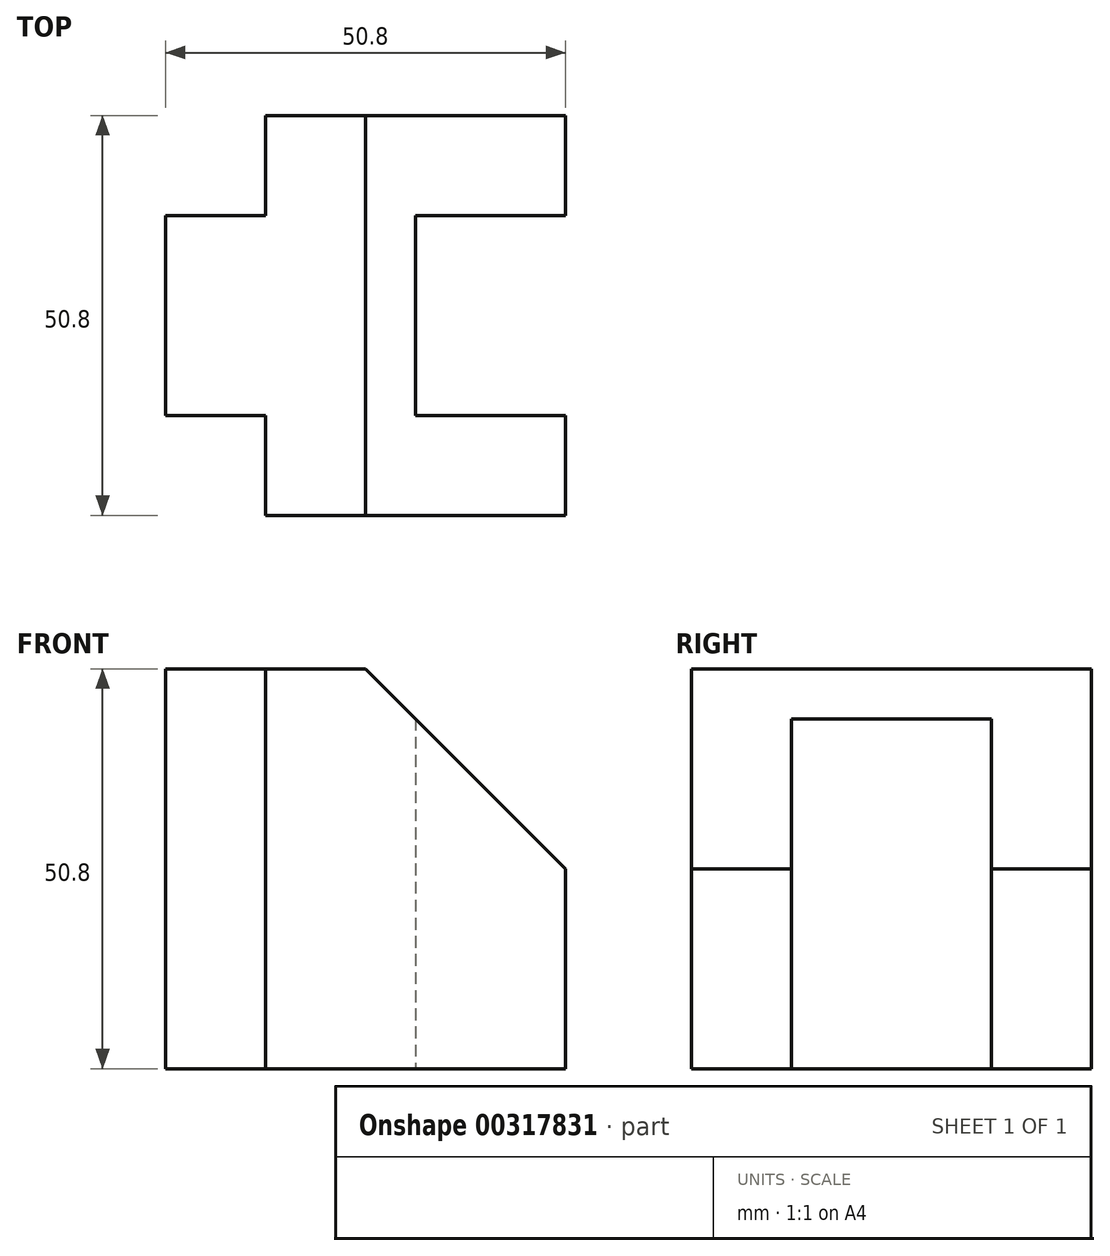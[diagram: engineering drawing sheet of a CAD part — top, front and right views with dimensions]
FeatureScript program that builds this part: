
annotation { "Feature Type Name" : "Feature", "Feature Type Description" : "" }
export const myFeature = defineFeature(function(context is Context, id is Id, definition is map)
    precondition{}
    {
        {
            var Q0;
            Q0=qCreatedBy(makeId("Front.planeOp"),FACE);
            var sketch = newSketch(context, id + "F0", { "sketchPlane" : qUnion([Q0])});
            skLineSegment(sketch, "E0", {"start": v(0, 0) * mm, "end": v(0, 50.8) * mm});
            skLineSegment(sketch, "E1", {"start": v(50.8, 0) * mm, "end": v(0, 0) * mm});
            skLineSegment(sketch, "E2", {"start": v(50.8, 0) * mm, "end": v(50.8, 25.4) * mm});
            skLineSegment(sketch, "E3", {"start": v(50.8, 25.4) * mm, "end": v(25.4, 50.8) * mm});
            skLineSegment(sketch, "E4", {"start": v(25.4, 50.8) * mm, "end": v(0, 50.8) * mm});
            skSolve(sketch);
        }
        {
            var Q0;
            Q0 = qSketchRegion(id + "F0", true);
            extrude(context, id + "F1", {"entities" : qUnion([Q0]), "depth" : 50.8 * mm});
        }
        {
            var Q0;
            Q0=makeQuery(id+"F1.opExtrude","SWEPT_FACE",FACE,{"disambiguationData":[OSD([sQuery(id+"F0.wireOp",EDGE,"E1")])]});
            var sketch = newSketch(context, id + "F2", { "sketchPlane" : qUnion([Q0])});
            skLineSegment(sketch, "E5", {"start": v(12.7, 50.8) * mm, "end": v(12.7, 38.1) * mm});
            skLineSegment(sketch, "E6", {"start": v(12.7, 38.1) * mm, "end": v(0, 38.1) * mm});
            skLineSegment(sketch, "E7", {"start": v(0, 12.7) * mm, "end": v(12.7, 12.7) * mm});
            skLineSegment(sketch, "E8", {"start": v(12.7, 12.7) * mm, "end": v(12.7, 0) * mm});
            skLineSegment(sketch, "E9", {"start": v(12.7, 0) * mm, "end": v(0, 0) * mm});
            skLineSegment(sketch, "E10", {"start": v(0, 0) * mm, "end": v(0, 12.7) * mm});
            skLineSegment(sketch, "E11", {"start": v(12.7, 50.8) * mm, "end": v(0, 50.8) * mm});
            skLineSegment(sketch, "E12", {"start": v(0, 50.8) * mm, "end": v(0, 38.1) * mm});
            skLineSegment(sketch, "E13", {"start": v(0, 0) * mm, "end": v(12.7, 0) * mm});
            skLineSegment(sketch, "E14", {"start": v(50.8, 38.1) * mm, "end": v(31.75, 38.1) * mm});
            skLineSegment(sketch, "E15", {"start": v(31.75, 38.1) * mm, "end": v(31.75, 12.7) * mm});
            skLineSegment(sketch, "E16", {"start": v(31.75, 12.7) * mm, "end": v(50.8, 12.7) * mm});
            skLineSegment(sketch, "E17", {"start": v(50.8, 12.7) * mm, "end": v(50.8, 38.1) * mm});
            skSolve(sketch);
        }
        {
            var Q0;
            Q0 = qSketchRegion(id + "F2", true);
            extrude(context, id + "F3", {"entities" : qUnion([Q0]), "operationType" : NewBodyOperationType.REMOVE, "endBound" : BoundingType.THROUGH_ALL, "oppositeDirection" : true, "depth" : 25.4 * mm});
        }
    });
